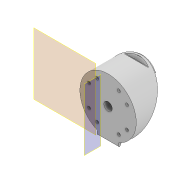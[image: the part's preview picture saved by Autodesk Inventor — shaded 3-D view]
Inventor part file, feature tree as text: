
AUTODESK INVENTOR PART (.ipt)
format: ipt  version: 2022 (Build 260153000, 153)  size: 209,920 bytes
history: native  units: in
note: dims shown in document units (in); Inventor stores cm internally (conversion verified against a paired STEP export)
features: reference x9, sketch x5, other x5, extrude x4, projected_geometry x4, plane x3, hole x1
ambient origin geometry x8: Origin, YZ Plane, XZ Plane, XY Plane, X Axis, Y Axis, Z Axis, Center Point
bodies: Solid1 (feature_tree)
feature tree (31):
  plane  "Work Plane1"
  plane  "Arbeitsebene5"
  extrude  "Extrusion1"  Depth=0.315in
  extrude  "Extrusion13"  Depth=0.0394in TaperAngle=0.0deg
  plane  "Arbeitsebene6"
  extrude  "Extrusion14"  Depth=0.0197in TaperAngle=0.0deg
  extrude  "Extrusion15"  TaperAngle=90.0deg  [1 undecoded]
  hole  "Bohrung3"  [1 undecoded]
  sketch  "Sketch1"  dims[d0=0.1969in d1=0.0in d2=0.315in]
  reference  "Reference1"
  reference  "Reference2"
  reference  "Reference3"
  reference  "Reference4"
  reference  "Reference5"
  reference  "Reference6"
  reference  "Reference7"
  reference  "Reference8"
  sketch  "Skizze17"  dims[d65=0.0079in d66=0.0394in d67=0.0in]
  reference  "Referenz30"
  projected_geometry  "Projizierte Kontur2"
  sketch  "Skizze18"  dims[d68=0.0197in d69=0.7874in d70=0.0in]
  projected_geometry  "Projizierte Kontur3"
  projected_geometry  "Projizierte Kontur4"
  sketch  "Skizze19"  dims[d71=135.0deg d72=90.0deg]
  projected_geometry  "Projizierte Kontur5"
  sketch  "Skizze20"  dims[d73=0.0197in d74=0.0in d75=0.0in d76=0.1102in d77=0.2362in d78=0.2559in d79=0.1181in d80=90.0deg d81=0.5512in d82=0.8108in]
  other  "Assembly1"
  other  "Assembly_MANATEE_V0_Manatee_middle2_v0_18:1"
  other  "Spectroscope_v0.iam"
  other  "00_Grating_1000linesPerMM:1"
  other  "Matchboxscope_bottom_v0:1"
note: 2 required parameter values undecoded (feature->parameter linkage not recoverable at this tier; creation-order binding heuristic only, values carry confidence <= 0.55)
